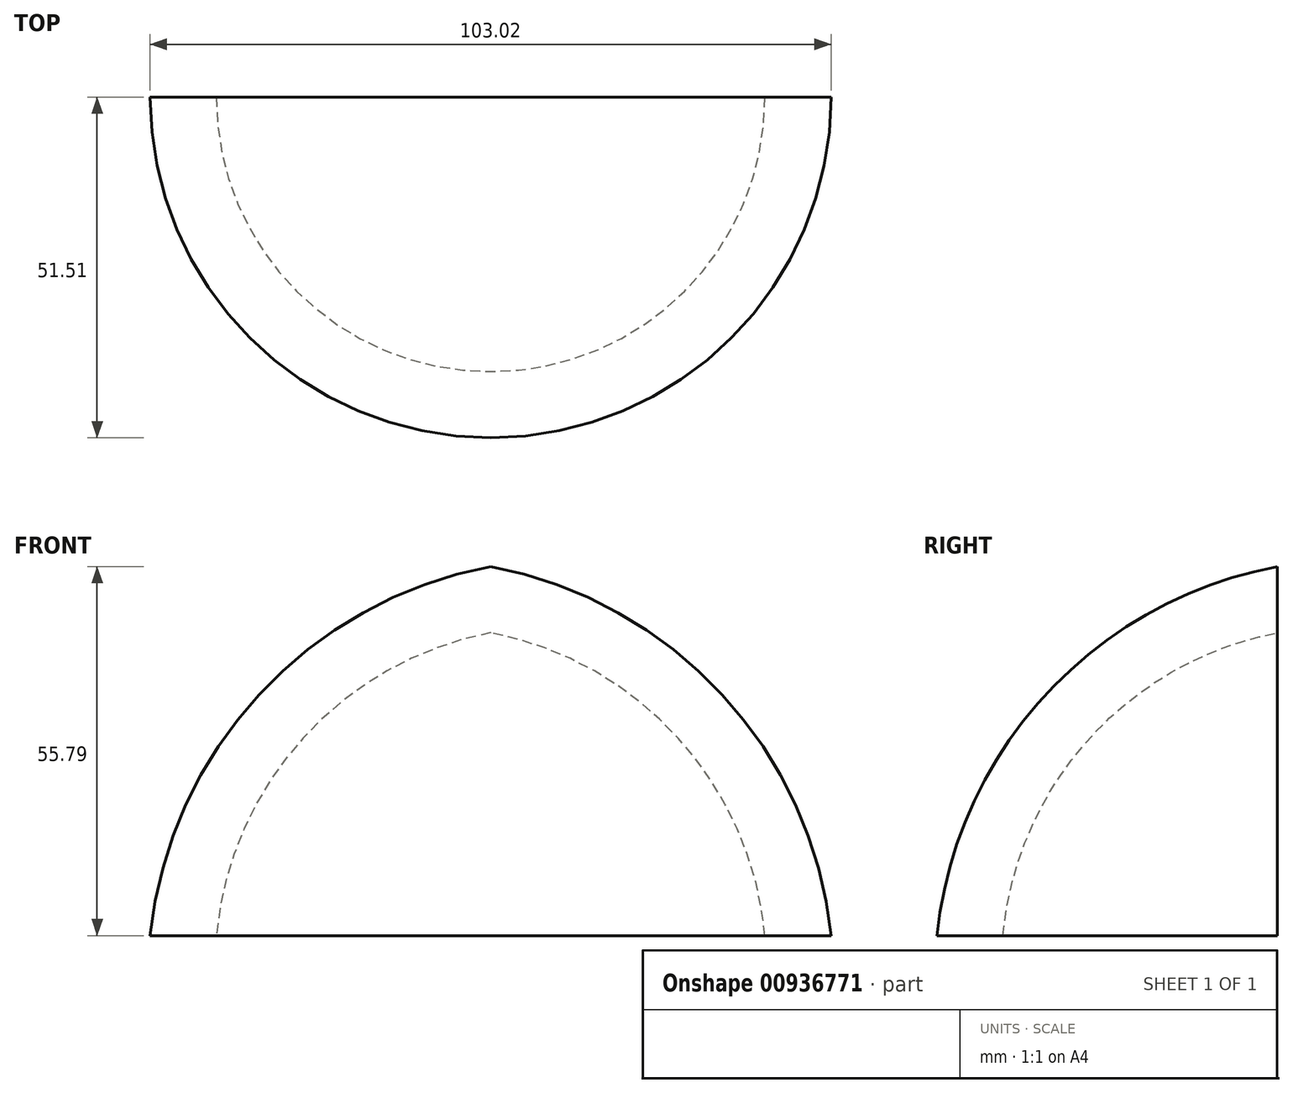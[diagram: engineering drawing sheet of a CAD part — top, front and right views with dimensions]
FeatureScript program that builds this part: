
annotation { "Feature Type Name" : "Feature", "Feature Type Description" : "" }
export const myFeature = defineFeature(function(context is Context, id is Id, definition is map)
    precondition{}
    {
        {
            var Q0;
            Q0=qCreatedBy(makeId("Front.planeOp"),FACE);
            var sketch = newSketch(context, id + "F0", { "sketchPlane" : qUnion([Q0])});
            skArc(sketch, "E0", {"start": v(51.51, 0) * mm, "mid": v(35.02, 36.45) * mm, "end": v(0, 55.8) * mm});
            skPoint(sketch, "E1.visualSharp", {"position": v(0, 0) * mm});
            skLineSegment(sketch, "E2", {"start": v(0, 55.8) * mm, "end": v(0, 45.8) * mm});
            skLineSegment(sketch, "E3", {"start": v(51.51, 0) * mm, "end": v(41.51, 0) * mm});
            skArc(sketch, "E4", {"start": v(41.51, 0) * mm, "mid": v(28.4, 29.83) * mm, "end": v(0, 45.8) * mm});
            skLineSegment(sketch, "E5", {"start": v(0, 55.8) * mm, "end": v(0, 0) * mm, "construction": true});
            skSolve(sketch);
        }
        {
            var Q0;
            Q0 = qSketchRegion(id + "F0", true);
            var Q1;
            Q1=sQuery(id+"F0.wireOp",EDGE,"E5");
            revolve(context, id + "F1", {"surfaceOperationType" : NewSurfaceOperationType.NEW, "entities" : qUnion([Q0]), "axis" : qUnion([Q1]), "revolveType" : RevolveType.ONE_DIRECTION, "angle" : 180 * degree});
        }
    });
